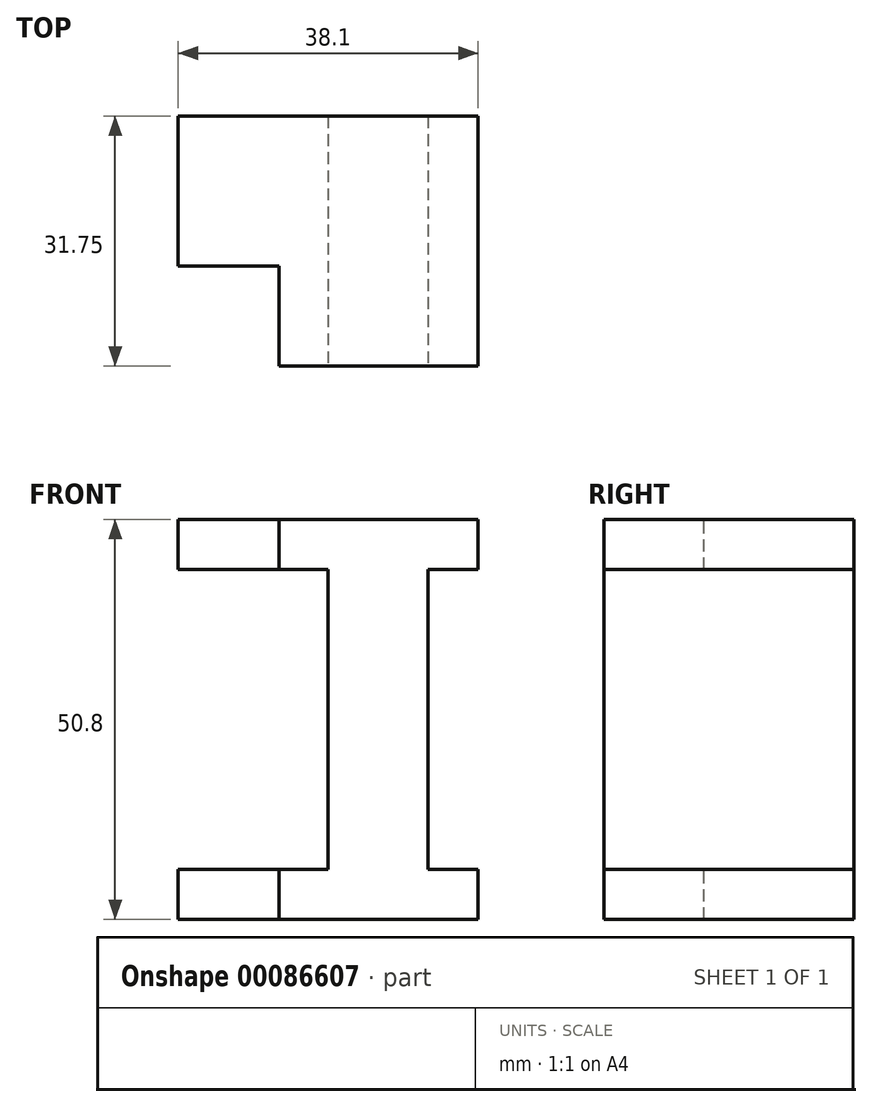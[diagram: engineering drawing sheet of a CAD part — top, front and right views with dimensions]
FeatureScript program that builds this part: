
annotation { "Feature Type Name" : "Feature", "Feature Type Description" : "" }
export const myFeature = defineFeature(function(context is Context, id is Id, definition is map)
    precondition{}
    {
        {
            var Q0;
            Q0=qCreatedBy(makeId("Front.planeOp"),FACE);
            var sketch = newSketch(context, id + "F0", { "sketchPlane" : qUnion([Q0])});
            skLineSegment(sketch, "E0", {"start": v(25.4, 25.4) * mm, "end": v(25.4, -25.4) * mm});
            skLineSegment(sketch, "E1", {"start": v(25.4, -25.4) * mm, "end": v(-25.4, -25.4) * mm});
            skLineSegment(sketch, "E2", {"start": v(-25.4, -25.4) * mm, "end": v(-25.4, 25.4) * mm});
            skLineSegment(sketch, "E3", {"start": v(-25.4, 25.4) * mm, "end": v(25.4, 25.4) * mm});
            skSolve(sketch);
        }
        {
            var Q0;
            Q0=makeQuery(id+"F0.imprint","IMPRINT",FACE,{"disambiguationData":[TD([[makeQuery(id+"F0.imprint","IMPRINT",EDGE,{"derivedFrom":sQuery(id+"F0.wireOp",EDGE,"E0")}),-1.0]])]});
            extrude(context, id + "F1", {"entities" : qUnion([Q0]), "depth" : 50.8 * mm});
        }
        {
            var Q0;
            Q0=qCreatedBy(makeId("Front.planeOp"),FACE);
            cPlane(context, id + "F2", {"entities" : qUnion([Q0]), "cplaneType" : CPlaneType.OFFSET, "offset" : 50.8 * mm, "width" : 152.4 * mm, "height" : 152.4 * mm});
        }
        {
            var Q0;
            Q0=qCreatedBy(makeId("Top.planeOp"),FACE);
            cPlane(context, id + "F3", {"entities" : qUnion([Q0]), "cplaneType" : CPlaneType.OFFSET, "offset" : 50.8 * mm, "width" : 152.4 * mm, "height" : 152.4 * mm});
        }
        {
            var Q0;
            Q0=qCreatedBy(id+"F2.planeOp",FACE);
            var sketch = newSketch(context, id + "F4", { "sketchPlane" : qUnion([Q0])});
            skLineSegment(sketch, "E4", {"start": v(-25.4, 25.4) * mm, "end": v(25.4, 25.4) * mm});
            skLineSegment(sketch, "E5", {"start": v(25.4, 25.4) * mm, "end": v(25.4, -25.4) * mm});
            skLineSegment(sketch, "E6", {"start": v(25.4, -25.4) * mm, "end": v(-25.4, -25.4) * mm});
            skLineSegment(sketch, "E7", {"start": v(-25.4, 25.4) * mm, "end": v(-25.4, -25.4) * mm});
            skLineSegment(sketch, "E8", {"start": v(-25.4, 25.4) * mm, "end": v(-25.4, 19.05) * mm});
            skLineSegment(sketch, "E9", {"start": v(-25.4, 19.05) * mm, "end": v(-6.35, 19.05) * mm});
            skLineSegment(sketch, "E10", {"start": v(-6.35, 19.05) * mm, "end": v(-6.35, -19.05) * mm});
            skLineSegment(sketch, "E11", {"start": v(-6.35, -19.05) * mm, "end": v(-25.4, -19.05) * mm});
            skLineSegment(sketch, "E12", {"start": v(-25.4, -19.05) * mm, "end": v(-25.4, -25.4) * mm});
            skLineSegment(sketch, "E13", {"start": v(25.4, -25.4) * mm, "end": v(25.4, -19.05) * mm});
            skLineSegment(sketch, "E14", {"start": v(25.4, -19.05) * mm, "end": v(6.35, -19.05) * mm});
            skLineSegment(sketch, "E15", {"start": v(6.35, -19.05) * mm, "end": v(6.35, 19.05) * mm});
            skLineSegment(sketch, "E16", {"start": v(6.35, 19.05) * mm, "end": v(25.4, 19.05) * mm});
            skLineSegment(sketch, "E17", {"start": v(-25.4, -25.4) * mm, "end": v(25.4, -25.4) * mm});
            skLineSegment(sketch, "E18", {"start": v(25.4, 19.05) * mm, "end": v(25.4, -19.05) * mm});
            skSolve(sketch);
        }
        {
            var Q0;
            {var subQ0=sQuery(id+"F4.wireOp",EDGE,"E10");Q0=makeQuery(id+"F4.imprint","IMPRINT",FACE,{"disambiguationData":[TD([[makeQuery(id+"F4.imprint","IMPRINT",EDGE,{"derivedFrom":subQ0}),-1.0]])]});}
            var Q1;
            Q1=makeQuery(id+"F4.imprint","IMPRINT",FACE,{"disambiguationData":[TD([[makeQuery(id+"F4.imprint","IMPRINT",EDGE,{"derivedFrom":sQuery(id+"F4.wireOp",EDGE,"E14")}),-1.0]])]});
            extrude(context, id + "F5", {"entities" : qUnion([Q0, Q1]), "operationType" : NewBodyOperationType.REMOVE, "oppositeDirection" : true, "depth" : 50.8 * mm});
        }
        {
            var Q0;
            Q0=qCreatedBy(id+"F3.planeOp",FACE);
            var sketch = newSketch(context, id + "F6", { "sketchPlane" : qUnion([Q0])});
            skLineSegment(sketch, "E19", {"start": v(25.4, 0) * mm, "end": v(25.4, -50.8) * mm});
            skLineSegment(sketch, "E20", {"start": v(25.4, -50.8) * mm, "end": v(-25.4, -50.8) * mm});
            skLineSegment(sketch, "E21", {"start": v(-25.4, -50.8) * mm, "end": v(-25.4, 0) * mm});
            skLineSegment(sketch, "E22", {"start": v(-25.4, 0) * mm, "end": v(25.4, 0) * mm});
            skLineSegment(sketch, "E23", {"start": v(12.66, -28.97) * mm, "end": v(12.66, -28.9) * mm});
            skLineSegment(sketch, "E24", {"start": v(12.66, 0) * mm, "end": v(25.4, 0) * mm});
            skLineSegment(sketch, "E25", {"start": v(-25.4, 0) * mm, "end": v(-25.4, -6.35) * mm});
            skLineSegment(sketch, "E26", {"start": v(-25.4, -6.35) * mm, "end": v(12.7, -6.35) * mm});
            skLineSegment(sketch, "E27", {"start": v(12.7, -6.35) * mm, "end": v(12.7, -38.1) * mm});
            skLineSegment(sketch, "E28", {"start": v(12.7, -38.1) * mm, "end": v(-12.6, -38.1) * mm});
            skLineSegment(sketch, "E29", {"start": v(-12.6, -38.1) * mm, "end": v(-12.6, -25.4) * mm});
            skLineSegment(sketch, "E30", {"start": v(-12.6, -25.4) * mm, "end": v(-25.4, -25.4) * mm});
            skLineSegment(sketch, "E31", {"start": v(-25.4, -25.4) * mm, "end": v(-25.4, -50.8) * mm});
            skSolve(sketch);
        }
        {
            var Q0;
            Q0=makeQuery(id+"F6.imprint","IMPRINT",FACE,{"disambiguationData":[TD([[makeQuery(id+"F6.imprint","IMPRINT",EDGE,{"derivedFrom":sQuery(id+"F6.wireOp",EDGE,"E21")}),-1.0]])]});
            extrude(context, id + "F7", {"entities" : qUnion([Q0]), "operationType" : NewBodyOperationType.REMOVE, "oppositeDirection" : true, "depth" : 76.2 * mm});
        }
    });
